# Revit family: HL307_2
name_source: partatom
category: Apparecchi idraulici
units: mm (PartAtom-declared; Revit-internal decimal feet)

## family parameters
Basato su piano di lavoro = No
Condiviso = No
Mantieni orientamento annotazione = No
Numero OmniClass = 23.45.55.17
Punto di calcolo locali = No
Quota connettore circolare = Usa diametro
Sempre verticale = Sì
Taglio con vuoti quando caricato = No
Tipo di parte = Normale
Titolo OmniClass = Mixing Faucets

## types (8) — shared parameters
Cold water inlet = 10 mm  [stored 0.0328084 ft]
Commenti sul tipo = Wall mounted widespread lavatory faucet with long spout
Connessione CW = No
Connessione HW = No
Connessione di scarico = No
Connessione di ventilazione = No
Descrizione = Wall mounted widespread lavatory faucet with long spout
Hot water inlet = 10 mm  [stored 0.0328084 ft]
Produttore = IB Rubinetterie S.p.A.
URL = https://www.weareib.it
zero-valued in all types: Prospetto di default

## per-type parameters (varying)
| type | Finishes surface | Immagine tipo | Modello |
| Chrome | IB_Chrome | HL307CC_2.jpg | HL307CC_2 |
| Antique Bronze | IB_Antique bronze | HL307BB_2.jpg | HL307BB_2 |
| Pale Gold | IB_Pale gold | HL307II_2.jpg | HL307II_2 |
| Brushed Gold | IB_brushed gold | HL307OS_2.jpg | HL307OS_2 |
| Platinum | IB_Platinum | HL307PL_2.jpg | HL307PL_2 |
| Antique Copper | IB_Antique copper | HL307RR_2.jpg | HL307RR_2 |
| Rose Gold | IB_Rose gold | HL307RS_2.jpg | HL307RS_2 |
| Brushed Nickel | IB_Brushed nickel | HL307SS_2.jpg | HL307SS_2 |

note: [stored X ft] marks values corroborated as IEEE doubles in the binary element streams (Revit-internal decimal feet)
